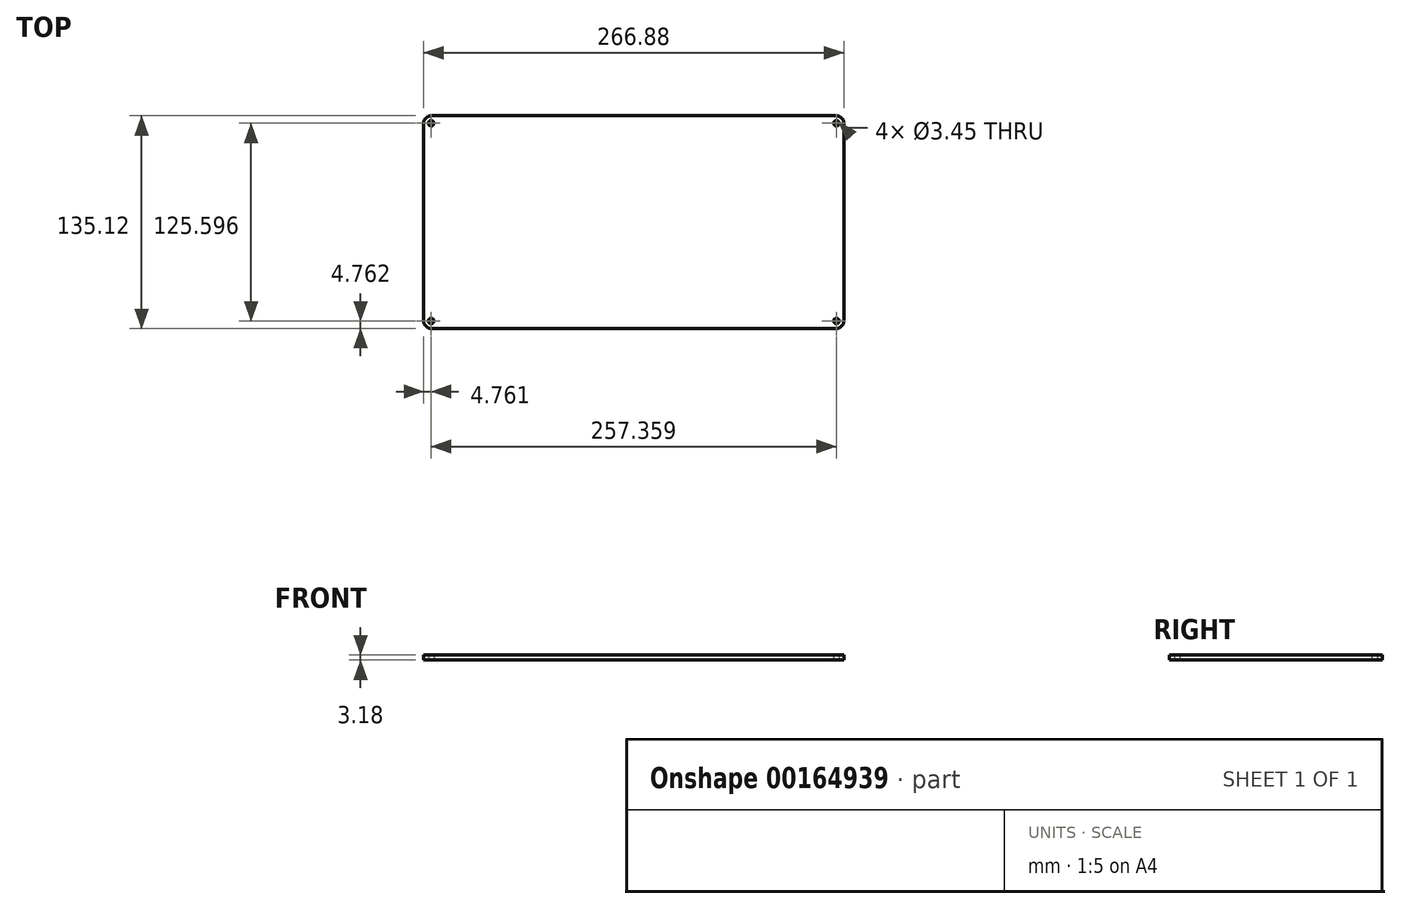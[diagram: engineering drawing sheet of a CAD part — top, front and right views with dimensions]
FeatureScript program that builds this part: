
annotation { "Feature Type Name" : "Feature", "Feature Type Description" : "" }
export const myFeature = defineFeature(function(context is Context, id is Id, definition is map)
    precondition{}
    {
        {
            var Q0;
            Q0=qCreatedBy(makeId("Top.planeOp"),FACE);
            var sketch = newSketch(context, id + "F0", { "sketchPlane" : qUnion([Q0])});
            skLineSegment(sketch, "E0.bottom", {"start": v(-128.68, 62.8) * mm, "end": v(128.68, 62.8) * mm, "construction": true});
            skLineSegment(sketch, "E0.top", {"start": v(-128.68, -62.8) * mm, "end": v(128.68, -62.8) * mm, "construction": true});
            skLineSegment(sketch, "E0.left", {"start": v(-128.68, 62.8) * mm, "end": v(-128.68, -62.8) * mm, "construction": true});
            skLineSegment(sketch, "E0.right", {"start": v(128.68, 62.8) * mm, "end": v(128.68, -62.8) * mm, "construction": true});
            skPoint(sketch, "E0.middle", {"position": v(0, 0) * mm});
            skLineSegment(sketch, "E1", {"start": v(-128.68, 0) * mm, "end": v(-133.44, 0) * mm, "construction": true});
            skLineSegment(sketch, "E2", {"start": v(0, 62.8) * mm, "end": v(0, 67.56) * mm, "construction": true});
            skLineSegment(sketch, "E3.bottom", {"start": v(-133.44, 67.56) * mm, "end": v(133.44, 67.56) * mm});
            skLineSegment(sketch, "E3.top", {"start": v(-133.44, -67.56) * mm, "end": v(133.44, -67.56) * mm});
            skLineSegment(sketch, "E3.left", {"start": v(-133.44, 67.56) * mm, "end": v(-133.44, -67.56) * mm});
            skLineSegment(sketch, "E3.right", {"start": v(133.44, 67.56) * mm, "end": v(133.44, -67.56) * mm});
            skCircle(sketch, "E4", {"center": v(-128.68, -62.8) * mm, "radius": 1.73 * mm});
            skCircle(sketch, "E5", {"center": v(-128.68, 62.8) * mm, "radius": 1.73 * mm});
            skCircle(sketch, "E6", {"center": v(128.68, 62.8) * mm, "radius": 1.73 * mm});
            skCircle(sketch, "E7", {"center": v(128.68, -62.8) * mm, "radius": 1.73 * mm});
            skSolve(sketch);
        }
        {
            var Q0;
            Q0 = qSketchRegion(id + "F0", true);
            extrude(context, id + "F1", {"entities" : qUnion([Q0]), "depth" : 3.17 * mm});
        }
        {
            var Q0;
            Q0=makeQuery(id+"F1.opExtrude","SWEPT_EDGE",EDGE,{"disambiguationData":[OSD([sQuery(id+"F0.wireOp",EDGE,"E3.top"),sQuery(id+"F0.wireOp",EDGE,"E3.right")])]});
            var Q1;
            Q1=makeQuery(id+"F1.opExtrude","SWEPT_EDGE",EDGE,{"disambiguationData":[OSD([sQuery(id+"F0.wireOp",EDGE,"E3.bottom"),sQuery(id+"F0.wireOp",EDGE,"E3.right")])]});
            var Q2;
            Q2=makeQuery(id+"F1.opExtrude","SWEPT_EDGE",EDGE,{"disambiguationData":[OSD([sQuery(id+"F0.wireOp",EDGE,"E3.top"),sQuery(id+"F0.wireOp",EDGE,"E3.left")])]});
            var Q3;
            Q3=makeQuery(id+"F1.opExtrude","SWEPT_EDGE",EDGE,{"disambiguationData":[OSD([sQuery(id+"F0.wireOp",EDGE,"E3.bottom"),sQuery(id+"F0.wireOp",EDGE,"E3.left")])]});
            fillet(context, id + "F2", {"entities" : qUnion([Q0, Q1, Q2, Q3]), "radius" : 4.76 * mm, "tangentPropagation" : true, "allowEdgeOverflow" : false});
        }
    });
